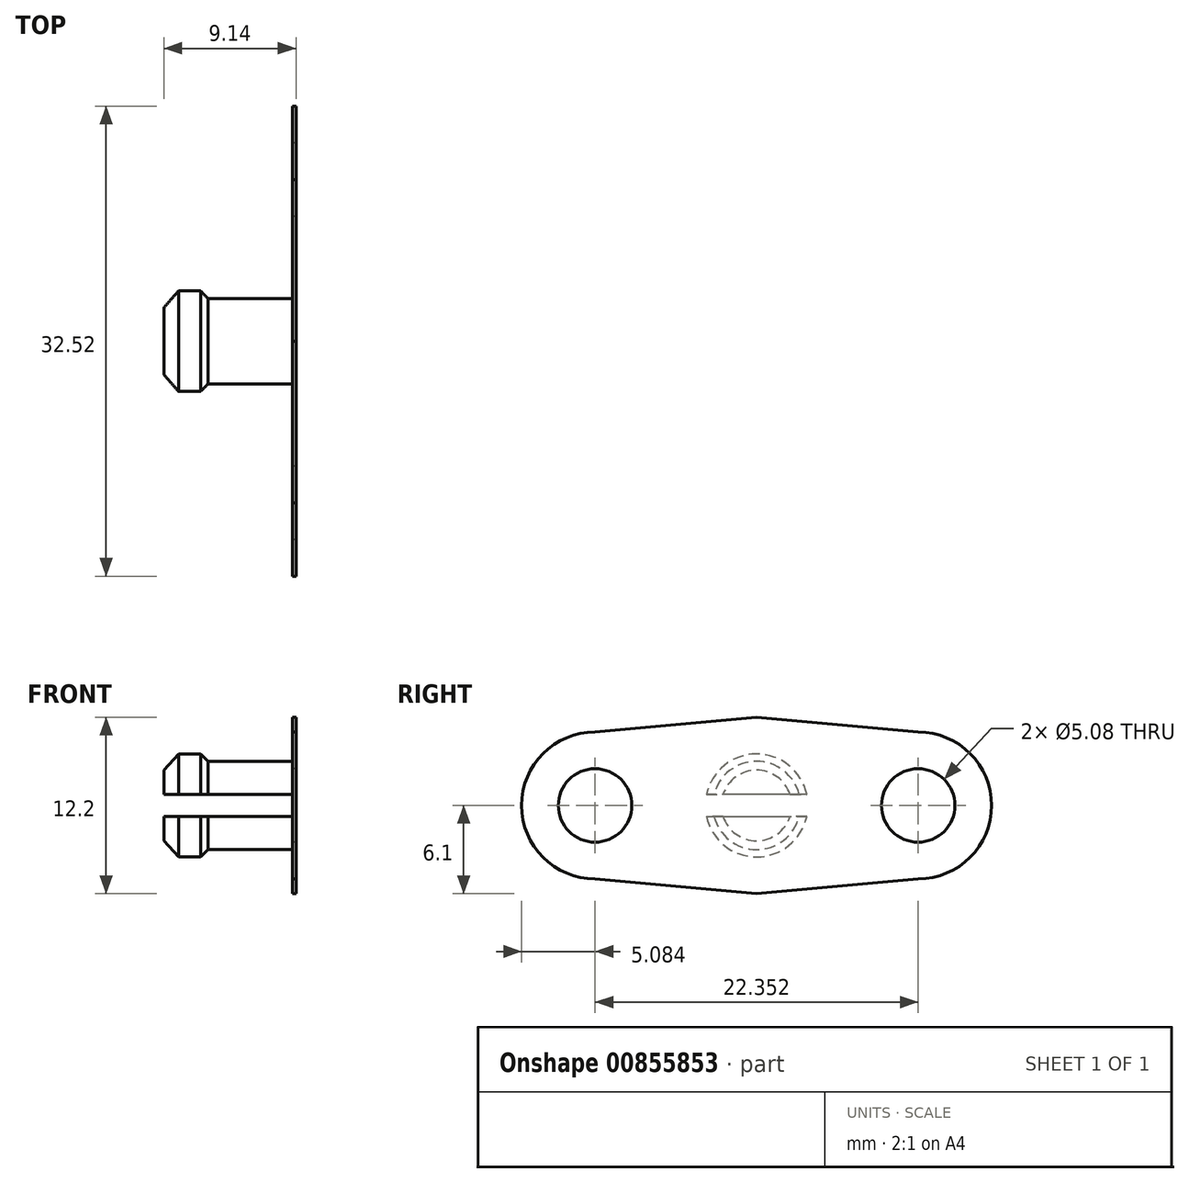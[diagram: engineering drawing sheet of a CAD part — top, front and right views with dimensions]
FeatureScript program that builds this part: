
annotation { "Feature Type Name" : "Feature", "Feature Type Description" : "" }
export const myFeature = defineFeature(function(context is Context, id is Id, definition is map)
    precondition{}
    {
        {
            assignVariable(context, id + "F0", {"name" : "Thickness", "anyValue" : .25});
        }
        {
            var Q0;
            Q0=qCreatedBy(makeId("Right.planeOp"),FACE);
            var sketch = newSketch(context, id + "F1", { "sketchPlane" : qUnion([Q0])});
            skArc(sketch, "E0", {"start": v(1.1, 6) * mm, "mid": v(0, 6.1) * mm, "end": v(-1.1, 6) * mm});
            skArc(sketch, "E1", {"start": v(11.18, -5.08) * mm, "mid": v(16.26, 0) * mm, "end": v(11.18, 5.08) * mm});
            skArc(sketch, "E2", {"start": v(-11.18, 5.08) * mm, "mid": v(-16.26, 0) * mm, "end": v(-11.18, -5.08) * mm});
            skLineSegment(sketch, "E3", {"start": v(0, 10.17) * mm, "end": v(0, -9.08) * mm, "construction": true});
            skLineSegment(sketch, "E4", {"start": v(11.18, 5.08) * mm, "end": v(0, 6.1) * mm});
            skLineSegment(sketch, "E5.MirrorCS", {"start": v(-11.18, 5.08) * mm, "end": v(0, 6.1) * mm});
            skLineSegment(sketch, "E6", {"start": v(20.86, 0) * mm, "end": v(-19.61, 0) * mm, "construction": true});
            skLineSegment(sketch, "E7.MirrorCS", {"start": v(-11.18, -5.08) * mm, "end": v(0, -6.1) * mm});
            skLineSegment(sketch, "E8.MirrorCS", {"start": v(11.18, -5.08) * mm, "end": v(0, -6.1) * mm});
            skArc(sketch, "E9.trimOffspring", {"start": v(-1.1, -6) * mm, "mid": v(0, -6.1) * mm, "end": v(1.1, -6) * mm});
            skCircle(sketch, "E10", {"center": v(11.18, 0) * mm, "radius": 2.54 * mm});
            skCircle(sketch, "E11", {"center": v(-11.18, 0) * mm, "radius": 2.54 * mm});
            skSolve(sketch);
        }
        {
            var Q0;
            {var subQ5=sQuery(id+"F1.wireOp",EDGE,"E1");Q0=makeQuery(id+"F1.imprint","IMPRINT",FACE,{"disambiguationData":[TD([[makeQuery(id+"F1.imprint","IMPRINT",EDGE,{"derivedFrom":subQ5}),1.0]])]});}
            extrude(context, id + "F2", {"entities" : qUnion([Q0]), "depth" : (getVariable(context, 'Thickness')) * mm, "offsetDistance" : 25.4 * mm});
        }
        {
            var Q0;
            Q0=qCreatedBy(makeId("Top.planeOp"),FACE);
            var sketch = newSketch(context, id + "F3", { "sketchPlane" : qUnion([Q0])});
            skLineSegment(sketch, "E12", {"start": v(0, 0) * mm, "end": v(-15.23, 0) * mm, "construction": true});
            skLineSegment(sketch, "E13.0", {"start": v(0, 11.18) * mm, "end": v(0, 0) * mm});
            skLineSegment(sketch, "E14", {"start": v(-8.9, 0) * mm, "end": v(-8.9, 2.44) * mm});
            skLineSegment(sketch, "E15", {"start": v(-8.9, 2.44) * mm, "end": v(-7.87, 3.56) * mm});
            skLineSegment(sketch, "E16", {"start": v(-7.87, 3.56) * mm, "end": v(-6.35, 3.56) * mm});
            skLineSegment(sketch, "E17", {"start": v(-6.35, 3.56) * mm, "end": v(-5.84, 3.05) * mm});
            skLineSegment(sketch, "E18", {"start": v(-5.84, 3.05) * mm, "end": v(0, 3.05) * mm});
            skLineSegment(sketch, "E19", {"start": v(-8.9, 0) * mm, "end": v(0, 0) * mm});
            skSolve(sketch);
        }
        {
            var Q0;
            Q0=makeQuery(id+"F3.imprint","IMPRINT",FACE,{"disambiguationData":[TD([[makeQuery(id+"F3.imprint","IMPRINT",EDGE,{"derivedFrom":sQuery(id+"F3.wireOp",EDGE,"E14")}),-1.0]])]});
            var Q1;
            Q1=sQuery(id+"F3.wireOp",EDGE,"E12");
            revolve(context, id + "F4", {"operationType" : NewBodyOperationType.ADD, "surfaceOperationType" : NewSurfaceOperationType.NEW, "entities" : qUnion([Q0]), "axis" : qUnion([Q1]), "revolveType" : RevolveType.FULL});
        }
        {
            var Q0;
            Q0=makeQuery(id+"F4.opRevolve","SWEPT_FACE",FACE,{"disambiguationData":[OSD([sQuery(id+"F3.wireOp",EDGE,"E14")])]});
            var sketch = newSketch(context, id + "F5", { "sketchPlane" : qUnion([Q0])});
            skLineSegment(sketch, "E20", {"start": v(-3.54, 0) * mm, "end": v(3.82, 0) * mm, "construction": true});
            skCircle(sketch, "E21.0", {"center": v(0, 0) * mm, "radius": 3.56 * mm});
            skLineSegment(sketch, "E22", {"start": v(-3.47, 0.76) * mm, "end": v(3.47, 0.76) * mm});
            skLineSegment(sketch, "E23", {"start": v(3.47, -0.76) * mm, "end": v(-3.47, -0.76) * mm});
            skSolve(sketch);
        }
        {
            var Q0;
            {var subQ0=sQuery(id+"F5.wireOp",EDGE,"E22");var subQ1=sQuery(id+"F5.wireOp",EDGE,"E21.0");var subQ2=makeQuery(id+"F5.imprint","INTERSECT",VERTEX,{"disambiguationData":[OD(0.0)],"derivedFrom":[subQ1,subQ0]});Q0=makeQuery(id+"F5.imprint","IMPRINT",FACE,{"disambiguationData":[TD([[makeQuery(id+"F5.imprint","IMPRINT",EDGE,{"disambiguationData":[TD([[subQ2,-1.0]])],"derivedFrom":subQ1}),1.0]])]});}
            var Q1;
            {var subQ0=sQuery(id+"F5.wireOp",EDGE,"E22");var subQ1=makeQuery(id+"F4.opRevolve","SWEPT_EDGE",EDGE,{"disambiguationData":[OSD([sQuery(id+"F3.wireOp",EDGE,"E14"),sQuery(id+"F3.wireOp",EDGE,"E15")])]});var subQ2=makeQuery(id+"F5.imprint","INTERSECT",VERTEX,{"disambiguationData":[OD(0.0)],"derivedFrom":[subQ1,subQ0]});Q1=makeQuery(id+"F5.imprint","IMPRINT",FACE,{"disambiguationData":[TD([[makeQuery(id+"F5.imprint","IMPRINT",EDGE,{"disambiguationData":[TD([[subQ2,-1.0]])],"derivedFrom":subQ0}),-1.0]])]});}
            var Q2;
            {var subQ0=sQuery(id+"F5.wireOp",EDGE,"E22");var subQ1=sQuery(id+"F5.wireOp",EDGE,"E21.0");var subQ2=makeQuery(id+"F5.imprint","INTERSECT",VERTEX,{"disambiguationData":[OD(1.0)],"derivedFrom":[subQ1,subQ0]});Q2=makeQuery(id+"F5.imprint","IMPRINT",FACE,{"disambiguationData":[TD([[makeQuery(id+"F5.imprint","IMPRINT",EDGE,{"disambiguationData":[TD([[subQ2,1.0]])],"derivedFrom":subQ1}),1.0]])]});}
            var Q3;
            Q3=makeQuery(id+"F2.opExtrude","CAP_FACE",FACE,{"disambiguationData":[OSD([sQuery(id+"F1.wireOp",EDGE,"E1"),sQuery(id+"F1.wireOp",EDGE,"E2"),sQuery(id+"F1.wireOp",EDGE,"E4"),sQuery(id+"F1.wireOp",EDGE,"E5.MirrorCS"),sQuery(id+"F1.wireOp",EDGE,"E7.MirrorCS"),sQuery(id+"F1.wireOp",EDGE,"E8.MirrorCS"),sQuery(id+"F1.wireOp",EDGE,"E10"),sQuery(id+"F1.wireOp",EDGE,"E11")])],"isStart":true});
            extrude(context, id + "F6", {"entities" : qUnion([Q0, Q1, Q2]), "operationType" : NewBodyOperationType.REMOVE, "endBound" : BoundingType.UP_TO_SURFACE, "oppositeDirection" : true, "depth" : 25.4 * mm, "endBoundEntityFace" : qUnion([Q3]), "offsetDistance" : 25.4 * mm});
        }
    });
